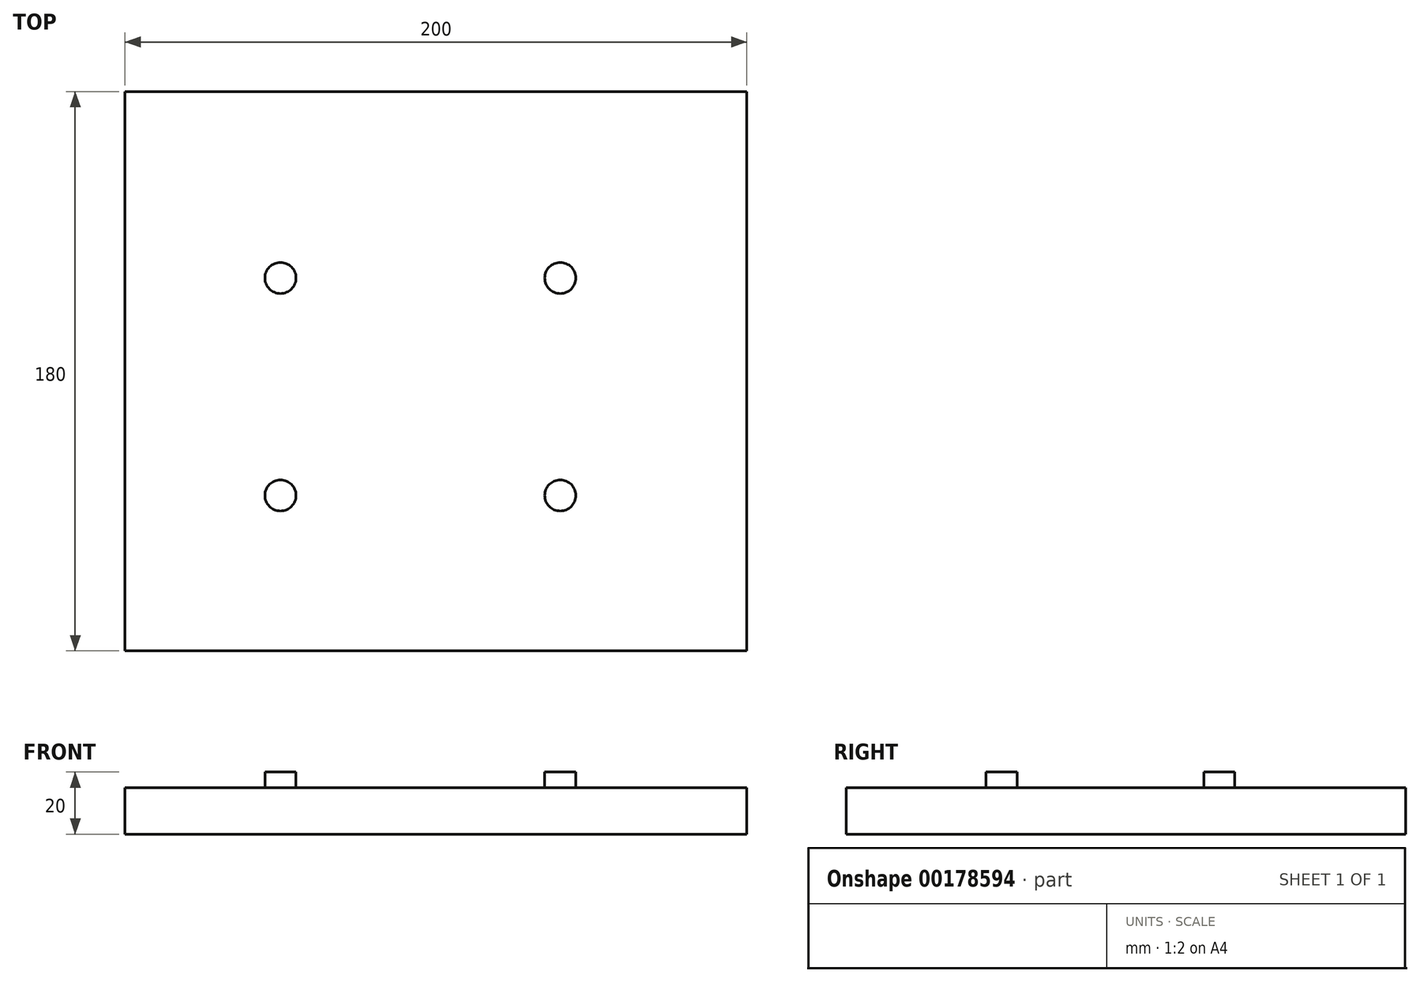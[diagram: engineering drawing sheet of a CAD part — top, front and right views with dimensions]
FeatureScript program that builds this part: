
annotation { "Feature Type Name" : "Feature", "Feature Type Description" : "" }
export const myFeature = defineFeature(function(context is Context, id is Id, definition is map)
    precondition{}
    {
        {
            var Q0;
            Q0=qCreatedBy(makeId("Top.planeOp"),FACE);
            var sketch = newSketch(context, id + "F0", { "sketchPlane" : qUnion([Q0])});
            skLineSegment(sketch, "E0.bottom", {"start": v(-100, 90) * mm, "end": v(100, 90) * mm});
            skLineSegment(sketch, "E0.top", {"start": v(-100, -90) * mm, "end": v(100, -90) * mm});
            skLineSegment(sketch, "E0.left", {"start": v(-100, 90) * mm, "end": v(-100, -90) * mm});
            skLineSegment(sketch, "E0.right", {"start": v(100, 90) * mm, "end": v(100, -90) * mm});
            skSolve(sketch);
        }
        {
            var Q0;
            Q0 = qSketchRegion(id + "F0", true);
            extrude(context, id + "F1", {"entities" : qUnion([Q0]), "depth" : 15 * mm});
        }
        {
            var Q0;
            Q0=makeQuery(id+"F1.opExtrude","CAP_FACE",FACE,{"disambiguationData":[OSD([sQuery(id+"F0.wireOp",EDGE,"E0.bottom"),sQuery(id+"F0.wireOp",EDGE,"E0.top"),sQuery(id+"F0.wireOp",EDGE,"E0.left"),sQuery(id+"F0.wireOp",EDGE,"E0.right")])],"isStart":false});
            var sketch = newSketch(context, id + "F2", { "sketchPlane" : qUnion([Q0])});
            skCircle(sketch, "E1", {"center": v(-50, 30) * mm, "radius": 5 * mm});
            skCircle(sketch, "E2", {"center": v(-50, -40) * mm, "radius": 5 * mm});
            skCircle(sketch, "E3", {"center": v(40, 30) * mm, "radius": 5 * mm});
            skCircle(sketch, "E4", {"center": v(40, -40) * mm, "radius": 5 * mm});
            skSolve(sketch);
        }
        {
            var Q0;
            Q0=makeQuery(id+"F2.imprint","IMPRINT",FACE,{"disambiguationData":[TD([[makeQuery(id+"F2.imprint","IMPRINT",EDGE,{"derivedFrom":sQuery(id+"F2.wireOp",EDGE,"E2")}),1.0]])]});
            var Q1;
            Q1=makeQuery(id+"F2.imprint","IMPRINT",FACE,{"disambiguationData":[TD([[makeQuery(id+"F2.imprint","IMPRINT",EDGE,{"derivedFrom":sQuery(id+"F2.wireOp",EDGE,"E4")}),1.0]])]});
            var Q2;
            Q2=makeQuery(id+"F2.imprint","IMPRINT",FACE,{"disambiguationData":[TD([[makeQuery(id+"F2.imprint","IMPRINT",EDGE,{"derivedFrom":sQuery(id+"F2.wireOp",EDGE,"E1")}),1.0]])]});
            var Q3;
            Q3=makeQuery(id+"F2.imprint","IMPRINT",FACE,{"disambiguationData":[TD([[makeQuery(id+"F2.imprint","IMPRINT",EDGE,{"derivedFrom":sQuery(id+"F2.wireOp",EDGE,"E3")}),1.0]])]});
            extrude(context, id + "F3", {"entities" : qUnion([Q0, Q1, Q2, Q3]), "operationType" : NewBodyOperationType.ADD, "depth" : 5 * mm});
        }
    });
